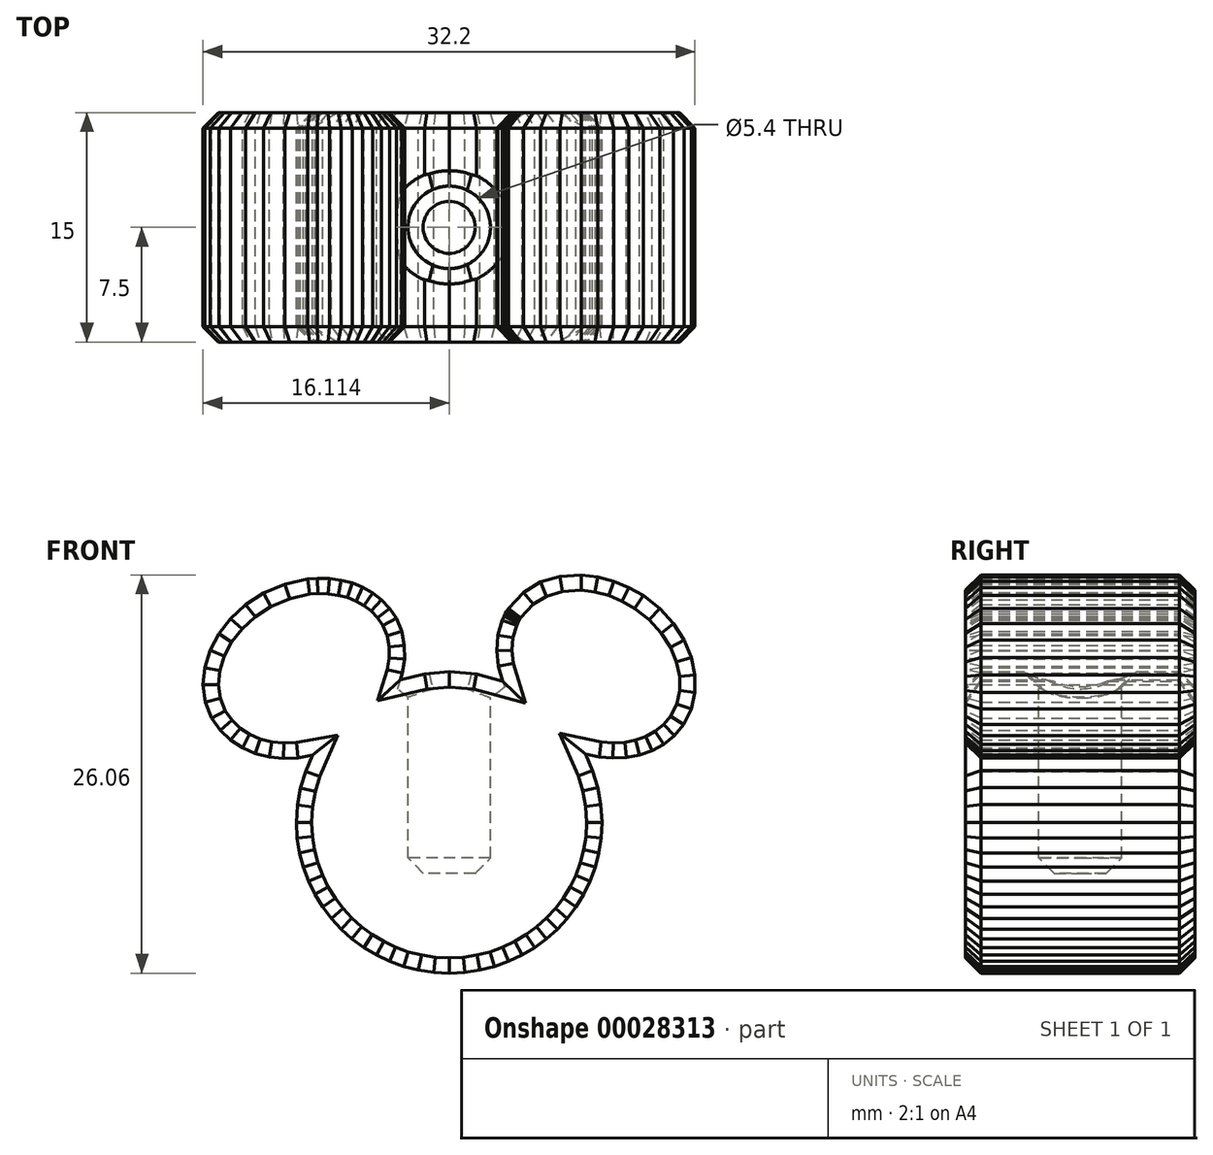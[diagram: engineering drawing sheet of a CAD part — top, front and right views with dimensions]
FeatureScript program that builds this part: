
annotation { "Feature Type Name" : "Feature", "Feature Type Description" : "" }
export const myFeature = defineFeature(function(context is Context, id is Id, definition is map)
    precondition{}
    {
        {
            var Q0;
            Q0=qCreatedBy(makeId("Front.planeOp"),FACE);
            var sketch = newSketch(context, id + "F0", { "sketchPlane" : qUnion([Q0])});
            skLineSegment(sketch, "E0", {"start": v(8.67, 13.03) * mm, "end": v(9.74, 12.9) * mm});
            skLineSegment(sketch, "E1", {"start": v(9.74, 12.9) * mm, "end": v(10.78, 12.63) * mm});
            skLineSegment(sketch, "E2", {"start": v(10.78, 12.63) * mm, "end": v(11.76, 12.21) * mm});
            skLineSegment(sketch, "E3", {"start": v(11.76, 12.21) * mm, "end": v(12.7, 11.68) * mm});
            skLineSegment(sketch, "E4", {"start": v(12.7, 11.68) * mm, "end": v(13.8, 10.82) * mm});
            skLineSegment(sketch, "E5", {"start": v(13.8, 10.82) * mm, "end": v(14.7, 9.84) * mm});
            skLineSegment(sketch, "E6", {"start": v(14.7, 9.84) * mm, "end": v(15.38, 8.77) * mm});
            skLineSegment(sketch, "E7", {"start": v(15.38, 8.77) * mm, "end": v(15.85, 7.64) * mm});
            skLineSegment(sketch, "E8", {"start": v(15.85, 7.64) * mm, "end": v(16.1, 6.48) * mm});
            skLineSegment(sketch, "E9", {"start": v(16.1, 6.48) * mm, "end": v(16.1, 5.34) * mm});
            skLineSegment(sketch, "E10", {"start": v(16.1, 5.34) * mm, "end": v(15.85, 4.25) * mm});
            skLineSegment(sketch, "E11", {"start": v(15.85, 4.25) * mm, "end": v(15.35, 3.24) * mm});
            skLineSegment(sketch, "E12", {"start": v(15.35, 3.24) * mm, "end": v(14.75, 2.52) * mm});
            skLineSegment(sketch, "E13", {"start": v(14.75, 2.52) * mm, "end": v(14.06, 1.96) * mm});
            skLineSegment(sketch, "E14", {"start": v(14.06, 1.96) * mm, "end": v(13.3, 1.53) * mm});
            skLineSegment(sketch, "E15", {"start": v(13.3, 1.53) * mm, "end": v(12.48, 1.25) * mm});
            skLineSegment(sketch, "E16", {"start": v(12.48, 1.25) * mm, "end": v(11.61, 1.09) * mm});
            skLineSegment(sketch, "E17", {"start": v(11.61, 1.09) * mm, "end": v(10.72, 1.05) * mm});
            skLineSegment(sketch, "E18", {"start": v(10.72, 1.05) * mm, "end": v(9.82, 1.12) * mm});
            skLineSegment(sketch, "E19", {"start": v(9.82, 1.12) * mm, "end": v(8.93, 1.3) * mm});
            skLineSegment(sketch, "E20", {"start": v(8.93, 1.3) * mm, "end": v(9.4, 0.24) * mm});
            skLineSegment(sketch, "E21", {"start": v(9.4, 0.24) * mm, "end": v(9.74, -0.87) * mm});
            skLineSegment(sketch, "E22", {"start": v(9.74, -0.87) * mm, "end": v(9.94, -2) * mm});
            skLineSegment(sketch, "E23", {"start": v(9.94, -2) * mm, "end": v(10.01, -3.17) * mm});
            skLineSegment(sketch, "E24", {"start": v(10.01, -3.17) * mm, "end": v(9.96, -4.18) * mm});
            skLineSegment(sketch, "E25", {"start": v(9.96, -4.18) * mm, "end": v(9.81, -5.16) * mm});
            skLineSegment(sketch, "E26", {"start": v(9.81, -5.16) * mm, "end": v(9.56, -6.1) * mm});
            skLineSegment(sketch, "E27", {"start": v(9.56, -6.1) * mm, "end": v(9.23, -7) * mm});
            skLineSegment(sketch, "E28", {"start": v(9.23, -7) * mm, "end": v(8.8, -7.87) * mm});
            skLineSegment(sketch, "E29", {"start": v(8.8, -7.87) * mm, "end": v(8.3, -8.68) * mm});
            skLineSegment(sketch, "E30", {"start": v(8.3, -8.68) * mm, "end": v(7.73, -9.44) * mm});
            skLineSegment(sketch, "E31", {"start": v(7.73, -9.44) * mm, "end": v(7.08, -10.14) * mm});
            skLineSegment(sketch, "E32", {"start": v(7.08, -10.14) * mm, "end": v(6.37, -10.78) * mm});
            skLineSegment(sketch, "E33", {"start": v(6.37, -10.78) * mm, "end": v(5.6, -11.35) * mm});
            skLineSegment(sketch, "E34", {"start": v(5.6, -11.35) * mm, "end": v(4.78, -11.84) * mm});
            skLineSegment(sketch, "E35", {"start": v(4.78, -11.84) * mm, "end": v(3.9, -12.26) * mm});
            skLineSegment(sketch, "E36", {"start": v(3.9, -12.26) * mm, "end": v(2.99, -12.59) * mm});
            skLineSegment(sketch, "E37", {"start": v(2.99, -12.59) * mm, "end": v(2.03, -12.83) * mm});
            skLineSegment(sketch, "E38", {"start": v(2.03, -12.83) * mm, "end": v(1.04, -12.98) * mm});
            skLineSegment(sketch, "E39", {"start": v(1.04, -12.98) * mm, "end": v(0.01, -13.03) * mm});
            skLineSegment(sketch, "E40", {"start": v(0.01, -13.03) * mm, "end": v(-1, -12.98) * mm});
            skLineSegment(sketch, "E41", {"start": v(-1, -12.98) * mm, "end": v(-2, -12.83) * mm});
            skLineSegment(sketch, "E42", {"start": v(-2, -12.83) * mm, "end": v(-2.96, -12.59) * mm});
            skLineSegment(sketch, "E43", {"start": v(-2.96, -12.59) * mm, "end": v(-3.88, -12.26) * mm});
            skLineSegment(sketch, "E44", {"start": v(-3.88, -12.26) * mm, "end": v(-4.75, -11.84) * mm});
            skLineSegment(sketch, "E45", {"start": v(-4.75, -11.84) * mm, "end": v(-5.58, -11.35) * mm});
            skLineSegment(sketch, "E46", {"start": v(-5.58, -11.35) * mm, "end": v(-6.35, -10.78) * mm});
            skLineSegment(sketch, "E47", {"start": v(-6.35, -10.78) * mm, "end": v(-7.06, -10.14) * mm});
            skLineSegment(sketch, "E48", {"start": v(-7.06, -10.14) * mm, "end": v(-7.7, -9.44) * mm});
            skLineSegment(sketch, "E49", {"start": v(-7.7, -9.44) * mm, "end": v(-8.28, -8.68) * mm});
            skLineSegment(sketch, "E50", {"start": v(-8.28, -8.68) * mm, "end": v(-8.78, -7.87) * mm});
            skLineSegment(sketch, "E51", {"start": v(-8.78, -7.87) * mm, "end": v(-9.2, -7) * mm});
            skLineSegment(sketch, "E52", {"start": v(-9.2, -7) * mm, "end": v(-9.54, -6.1) * mm});
            skLineSegment(sketch, "E53", {"start": v(-9.54, -6.1) * mm, "end": v(-9.78, -5.16) * mm});
            skLineSegment(sketch, "E54", {"start": v(-9.78, -5.16) * mm, "end": v(-9.93, -4.18) * mm});
            skLineSegment(sketch, "E55", {"start": v(-9.93, -4.18) * mm, "end": v(-9.99, -3.17) * mm});
            skLineSegment(sketch, "E56", {"start": v(-9.99, -3.17) * mm, "end": v(-9.92, -2.03) * mm});
            skLineSegment(sketch, "E57", {"start": v(-9.92, -2.03) * mm, "end": v(-9.72, -0.9) * mm});
            skLineSegment(sketch, "E58", {"start": v(-9.72, -0.9) * mm, "end": v(-9.38, 0.18) * mm});
            skLineSegment(sketch, "E59", {"start": v(-9.38, 0.18) * mm, "end": v(-8.94, 1.23) * mm});
            skLineSegment(sketch, "E60", {"start": v(-8.94, 1.23) * mm, "end": v(-9.89, 1.06) * mm});
            skLineSegment(sketch, "E61", {"start": v(-9.89, 1.06) * mm, "end": v(-10.84, 1.03) * mm});
            skLineSegment(sketch, "E62", {"start": v(-10.84, 1.03) * mm, "end": v(-11.77, 1.12) * mm});
            skLineSegment(sketch, "E63", {"start": v(-11.77, 1.12) * mm, "end": v(-12.67, 1.35) * mm});
            skLineSegment(sketch, "E64", {"start": v(-12.67, 1.35) * mm, "end": v(-13.52, 1.71) * mm});
            skLineSegment(sketch, "E65", {"start": v(-13.52, 1.71) * mm, "end": v(-14.3, 2.22) * mm});
            skLineSegment(sketch, "E66", {"start": v(-14.3, 2.22) * mm, "end": v(-14.97, 2.87) * mm});
            skLineSegment(sketch, "E67", {"start": v(-14.97, 2.87) * mm, "end": v(-15.54, 3.67) * mm});
            skLineSegment(sketch, "E68", {"start": v(-15.54, 3.67) * mm, "end": v(-15.95, 4.72) * mm});
            skLineSegment(sketch, "E69", {"start": v(-15.95, 4.72) * mm, "end": v(-16.1, 5.83) * mm});
            skLineSegment(sketch, "E70", {"start": v(-16.1, 5.83) * mm, "end": v(-15.99, 6.97) * mm});
            skLineSegment(sketch, "E71", {"start": v(-15.99, 6.97) * mm, "end": v(-15.64, 8.1) * mm});
            skLineSegment(sketch, "E72", {"start": v(-15.64, 8.1) * mm, "end": v(-15.07, 9.17) * mm});
            skLineSegment(sketch, "E73", {"start": v(-15.07, 9.17) * mm, "end": v(-14.29, 10.18) * mm});
            skLineSegment(sketch, "E74", {"start": v(-14.29, 10.18) * mm, "end": v(-13.3, 11.08) * mm});
            skLineSegment(sketch, "E75", {"start": v(-13.3, 11.08) * mm, "end": v(-12.14, 11.84) * mm});
            skLineSegment(sketch, "E76", {"start": v(-12.14, 11.84) * mm, "end": v(-10.74, 12.44) * mm});
            skLineSegment(sketch, "E77", {"start": v(-10.74, 12.44) * mm, "end": v(-9.26, 12.77) * mm});
            skLineSegment(sketch, "E78", {"start": v(-9.26, 12.77) * mm, "end": v(-8.62, 12.82) * mm});
            skLineSegment(sketch, "E79", {"start": v(-8.62, 12.82) * mm, "end": v(-7.83, 12.8) * mm});
            skLineSegment(sketch, "E80", {"start": v(-7.83, 12.8) * mm, "end": v(-7.07, 12.69) * mm});
            skLineSegment(sketch, "E81", {"start": v(-7.07, 12.69) * mm, "end": v(-6.34, 12.5) * mm});
            skLineSegment(sketch, "E82", {"start": v(-6.34, 12.5) * mm, "end": v(-5.65, 12.23) * mm});
            skLineSegment(sketch, "E83", {"start": v(-5.65, 12.23) * mm, "end": v(-5, 11.86) * mm});
            skLineSegment(sketch, "E84", {"start": v(-5, 11.86) * mm, "end": v(-4.42, 11.4) * mm});
            skLineSegment(sketch, "E85", {"start": v(-4.42, 11.4) * mm, "end": v(-3.9, 10.85) * mm});
            skLineSegment(sketch, "E86", {"start": v(-3.9, 10.85) * mm, "end": v(-3.45, 10.19) * mm});
            skLineSegment(sketch, "E87", {"start": v(-3.45, 10.19) * mm, "end": v(-3.1, 9.33) * mm});
            skLineSegment(sketch, "E88", {"start": v(-3.1, 9.33) * mm, "end": v(-2.92, 8.43) * mm});
            skLineSegment(sketch, "E89", {"start": v(-2.92, 8.43) * mm, "end": v(-2.91, 7.52) * mm});
            skLineSegment(sketch, "E90", {"start": v(-2.91, 7.52) * mm, "end": v(-3.06, 6.6) * mm});
            skLineSegment(sketch, "E91", {"start": v(-3.06, 6.6) * mm, "end": v(-3.2, 6.18) * mm});
            skLineSegment(sketch, "E92", {"start": v(-3.2, 6.18) * mm, "end": v(-1.61, 6.56) * mm});
            skLineSegment(sketch, "E93", {"start": v(-1.61, 6.56) * mm, "end": v(0.01, 6.7) * mm});
            skLineSegment(sketch, "E94", {"start": v(0.01, 6.7) * mm, "end": v(1.8, 6.54) * mm});
            skLineSegment(sketch, "E95", {"start": v(1.8, 6.54) * mm, "end": v(3.52, 6.07) * mm});
            skLineSegment(sketch, "E96", {"start": v(3.52, 6.07) * mm, "end": v(3.23, 7.05) * mm});
            skLineSegment(sketch, "E97", {"start": v(3.23, 7.05) * mm, "end": v(3.12, 8.08) * mm});
            skLineSegment(sketch, "E98", {"start": v(3.12, 8.08) * mm, "end": v(3.2, 9.1) * mm});
            skLineSegment(sketch, "E99", {"start": v(3.2, 9.1) * mm, "end": v(3.5, 10.08) * mm});
            skLineSegment(sketch, "E100", {"start": v(3.5, 10.08) * mm, "end": v(3.6, 10.31) * mm});
            skLineSegment(sketch, "E101", {"start": v(3.6, 10.31) * mm, "end": v(3.69, 10.49) * mm});
            skLineSegment(sketch, "E102", {"start": v(3.69, 10.49) * mm, "end": v(3.78, 10.65) * mm});
            skLineSegment(sketch, "E103", {"start": v(3.78, 10.65) * mm, "end": v(3.9, 10.83) * mm});
            skLineSegment(sketch, "E104", {"start": v(3.9, 10.83) * mm, "end": v(4.87, 11.9) * mm});
            skLineSegment(sketch, "E105", {"start": v(4.87, 11.9) * mm, "end": v(5.98, 12.57) * mm});
            skLineSegment(sketch, "E106", {"start": v(5.98, 12.57) * mm, "end": v(7.25, 12.92) * mm});
            skLineSegment(sketch, "E107", {"start": v(7.25, 12.92) * mm, "end": v(8.67, 13.03) * mm});
            skSolve(sketch);
        }
        {
            var Q0;
            Q0 = qSketchRegion(id + "F0", true);
            extrude(context, id + "F1", {"entities" : qUnion([Q0]), "depth" : 15 * mm});
        }
        {
            var Q0;
            Q0=makeQuery(id+"F1.opExtrude","CAP_FACE",FACE,{"disambiguationData":[OSD([sQuery(id+"F0.wireOp",EDGE,"E0"),sQuery(id+"F0.wireOp",EDGE,"E1"),sQuery(id+"F0.wireOp",EDGE,"E2"),sQuery(id+"F0.wireOp",EDGE,"E3"),sQuery(id+"F0.wireOp",EDGE,"E4"),sQuery(id+"F0.wireOp",EDGE,"E5"),sQuery(id+"F0.wireOp",EDGE,"E6"),sQuery(id+"F0.wireOp",EDGE,"E7"),sQuery(id+"F0.wireOp",EDGE,"E8"),sQuery(id+"F0.wireOp",EDGE,"E9"),sQuery(id+"F0.wireOp",EDGE,"E10"),sQuery(id+"F0.wireOp",EDGE,"E11"),sQuery(id+"F0.wireOp",EDGE,"E12"),sQuery(id+"F0.wireOp",EDGE,"E13"),sQuery(id+"F0.wireOp",EDGE,"E14"),sQuery(id+"F0.wireOp",EDGE,"E15"),sQuery(id+"F0.wireOp",EDGE,"E16"),sQuery(id+"F0.wireOp",EDGE,"E17"),sQuery(id+"F0.wireOp",EDGE,"E18"),sQuery(id+"F0.wireOp",EDGE,"E19"),sQuery(id+"F0.wireOp",EDGE,"E20"),sQuery(id+"F0.wireOp",EDGE,"E21"),sQuery(id+"F0.wireOp",EDGE,"E22"),sQuery(id+"F0.wireOp",EDGE,"E23"),sQuery(id+"F0.wireOp",EDGE,"E24"),sQuery(id+"F0.wireOp",EDGE,"E25"),sQuery(id+"F0.wireOp",EDGE,"E26"),sQuery(id+"F0.wireOp",EDGE,"E27"),sQuery(id+"F0.wireOp",EDGE,"E28"),sQuery(id+"F0.wireOp",EDGE,"E29"),sQuery(id+"F0.wireOp",EDGE,"E30"),sQuery(id+"F0.wireOp",EDGE,"E31"),sQuery(id+"F0.wireOp",EDGE,"E32"),sQuery(id+"F0.wireOp",EDGE,"E33"),sQuery(id+"F0.wireOp",EDGE,"E34"),sQuery(id+"F0.wireOp",EDGE,"E35"),sQuery(id+"F0.wireOp",EDGE,"E36"),sQuery(id+"F0.wireOp",EDGE,"E37"),sQuery(id+"F0.wireOp",EDGE,"E38"),sQuery(id+"F0.wireOp",EDGE,"E39"),sQuery(id+"F0.wireOp",EDGE,"E40"),sQuery(id+"F0.wireOp",EDGE,"E41"),sQuery(id+"F0.wireOp",EDGE,"E42"),sQuery(id+"F0.wireOp",EDGE,"E43"),sQuery(id+"F0.wireOp",EDGE,"E44"),sQuery(id+"F0.wireOp",EDGE,"E45"),sQuery(id+"F0.wireOp",EDGE,"E46"),sQuery(id+"F0.wireOp",EDGE,"E47"),sQuery(id+"F0.wireOp",EDGE,"E48"),sQuery(id+"F0.wireOp",EDGE,"E49"),sQuery(id+"F0.wireOp",EDGE,"E50"),sQuery(id+"F0.wireOp",EDGE,"E51"),sQuery(id+"F0.wireOp",EDGE,"E52"),sQuery(id+"F0.wireOp",EDGE,"E53"),sQuery(id+"F0.wireOp",EDGE,"E54"),sQuery(id+"F0.wireOp",EDGE,"E55"),sQuery(id+"F0.wireOp",EDGE,"E56"),sQuery(id+"F0.wireOp",EDGE,"E57"),sQuery(id+"F0.wireOp",EDGE,"E58"),sQuery(id+"F0.wireOp",EDGE,"E59"),sQuery(id+"F0.wireOp",EDGE,"E60"),sQuery(id+"F0.wireOp",EDGE,"E61"),sQuery(id+"F0.wireOp",EDGE,"E62"),sQuery(id+"F0.wireOp",EDGE,"E63"),sQuery(id+"F0.wireOp",EDGE,"E64"),sQuery(id+"F0.wireOp",EDGE,"E65"),sQuery(id+"F0.wireOp",EDGE,"E66"),sQuery(id+"F0.wireOp",EDGE,"E67"),sQuery(id+"F0.wireOp",EDGE,"E68"),sQuery(id+"F0.wireOp",EDGE,"E69"),sQuery(id+"F0.wireOp",EDGE,"E70"),sQuery(id+"F0.wireOp",EDGE,"E71"),sQuery(id+"F0.wireOp",EDGE,"E72"),sQuery(id+"F0.wireOp",EDGE,"E73"),sQuery(id+"F0.wireOp",EDGE,"E74"),sQuery(id+"F0.wireOp",EDGE,"E75"),sQuery(id+"F0.wireOp",EDGE,"E76"),sQuery(id+"F0.wireOp",EDGE,"E77"),sQuery(id+"F0.wireOp",EDGE,"E78"),sQuery(id+"F0.wireOp",EDGE,"E79"),sQuery(id+"F0.wireOp",EDGE,"E80"),sQuery(id+"F0.wireOp",EDGE,"E81"),sQuery(id+"F0.wireOp",EDGE,"E82"),sQuery(id+"F0.wireOp",EDGE,"E83"),sQuery(id+"F0.wireOp",EDGE,"E84"),sQuery(id+"F0.wireOp",EDGE,"E85"),sQuery(id+"F0.wireOp",EDGE,"E86"),sQuery(id+"F0.wireOp",EDGE,"E87"),sQuery(id+"F0.wireOp",EDGE,"E88"),sQuery(id+"F0.wireOp",EDGE,"E89"),sQuery(id+"F0.wireOp",EDGE,"E90"),sQuery(id+"F0.wireOp",EDGE,"E91"),sQuery(id+"F0.wireOp",EDGE,"E92"),sQuery(id+"F0.wireOp",EDGE,"E93"),sQuery(id+"F0.wireOp",EDGE,"E94"),sQuery(id+"F0.wireOp",EDGE,"E95"),sQuery(id+"F0.wireOp",EDGE,"E96"),sQuery(id+"F0.wireOp",EDGE,"E97"),sQuery(id+"F0.wireOp",EDGE,"E98"),sQuery(id+"F0.wireOp",EDGE,"E99"),sQuery(id+"F0.wireOp",EDGE,"E100"),sQuery(id+"F0.wireOp",EDGE,"E101"),sQuery(id+"F0.wireOp",EDGE,"E102"),sQuery(id+"F0.wireOp",EDGE,"E103"),sQuery(id+"F0.wireOp",EDGE,"E104"),sQuery(id+"F0.wireOp",EDGE,"E105"),sQuery(id+"F0.wireOp",EDGE,"E106"),sQuery(id+"F0.wireOp",EDGE,"E107")])],"isStart":false});
            var Q1;
            Q1=makeQuery(id+"F1.opExtrude","CAP_FACE",FACE,{"disambiguationData":[OSD([sQuery(id+"F0.wireOp",EDGE,"E0"),sQuery(id+"F0.wireOp",EDGE,"E1"),sQuery(id+"F0.wireOp",EDGE,"E2"),sQuery(id+"F0.wireOp",EDGE,"E3"),sQuery(id+"F0.wireOp",EDGE,"E4"),sQuery(id+"F0.wireOp",EDGE,"E5"),sQuery(id+"F0.wireOp",EDGE,"E6"),sQuery(id+"F0.wireOp",EDGE,"E7"),sQuery(id+"F0.wireOp",EDGE,"E8"),sQuery(id+"F0.wireOp",EDGE,"E9"),sQuery(id+"F0.wireOp",EDGE,"E10"),sQuery(id+"F0.wireOp",EDGE,"E11"),sQuery(id+"F0.wireOp",EDGE,"E12"),sQuery(id+"F0.wireOp",EDGE,"E13"),sQuery(id+"F0.wireOp",EDGE,"E14"),sQuery(id+"F0.wireOp",EDGE,"E15"),sQuery(id+"F0.wireOp",EDGE,"E16"),sQuery(id+"F0.wireOp",EDGE,"E17"),sQuery(id+"F0.wireOp",EDGE,"E18"),sQuery(id+"F0.wireOp",EDGE,"E19"),sQuery(id+"F0.wireOp",EDGE,"E20"),sQuery(id+"F0.wireOp",EDGE,"E21"),sQuery(id+"F0.wireOp",EDGE,"E22"),sQuery(id+"F0.wireOp",EDGE,"E23"),sQuery(id+"F0.wireOp",EDGE,"E24"),sQuery(id+"F0.wireOp",EDGE,"E25"),sQuery(id+"F0.wireOp",EDGE,"E26"),sQuery(id+"F0.wireOp",EDGE,"E27"),sQuery(id+"F0.wireOp",EDGE,"E28"),sQuery(id+"F0.wireOp",EDGE,"E29"),sQuery(id+"F0.wireOp",EDGE,"E30"),sQuery(id+"F0.wireOp",EDGE,"E31"),sQuery(id+"F0.wireOp",EDGE,"E32"),sQuery(id+"F0.wireOp",EDGE,"E33"),sQuery(id+"F0.wireOp",EDGE,"E34"),sQuery(id+"F0.wireOp",EDGE,"E35"),sQuery(id+"F0.wireOp",EDGE,"E36"),sQuery(id+"F0.wireOp",EDGE,"E37"),sQuery(id+"F0.wireOp",EDGE,"E38"),sQuery(id+"F0.wireOp",EDGE,"E39"),sQuery(id+"F0.wireOp",EDGE,"E40"),sQuery(id+"F0.wireOp",EDGE,"E41"),sQuery(id+"F0.wireOp",EDGE,"E42"),sQuery(id+"F0.wireOp",EDGE,"E43"),sQuery(id+"F0.wireOp",EDGE,"E44"),sQuery(id+"F0.wireOp",EDGE,"E45"),sQuery(id+"F0.wireOp",EDGE,"E46"),sQuery(id+"F0.wireOp",EDGE,"E47"),sQuery(id+"F0.wireOp",EDGE,"E48"),sQuery(id+"F0.wireOp",EDGE,"E49"),sQuery(id+"F0.wireOp",EDGE,"E50"),sQuery(id+"F0.wireOp",EDGE,"E51"),sQuery(id+"F0.wireOp",EDGE,"E52"),sQuery(id+"F0.wireOp",EDGE,"E53"),sQuery(id+"F0.wireOp",EDGE,"E54"),sQuery(id+"F0.wireOp",EDGE,"E55"),sQuery(id+"F0.wireOp",EDGE,"E56"),sQuery(id+"F0.wireOp",EDGE,"E57"),sQuery(id+"F0.wireOp",EDGE,"E58"),sQuery(id+"F0.wireOp",EDGE,"E59"),sQuery(id+"F0.wireOp",EDGE,"E60"),sQuery(id+"F0.wireOp",EDGE,"E61"),sQuery(id+"F0.wireOp",EDGE,"E62"),sQuery(id+"F0.wireOp",EDGE,"E63"),sQuery(id+"F0.wireOp",EDGE,"E64"),sQuery(id+"F0.wireOp",EDGE,"E65"),sQuery(id+"F0.wireOp",EDGE,"E66"),sQuery(id+"F0.wireOp",EDGE,"E67"),sQuery(id+"F0.wireOp",EDGE,"E68"),sQuery(id+"F0.wireOp",EDGE,"E69"),sQuery(id+"F0.wireOp",EDGE,"E70"),sQuery(id+"F0.wireOp",EDGE,"E71"),sQuery(id+"F0.wireOp",EDGE,"E72"),sQuery(id+"F0.wireOp",EDGE,"E73"),sQuery(id+"F0.wireOp",EDGE,"E74"),sQuery(id+"F0.wireOp",EDGE,"E75"),sQuery(id+"F0.wireOp",EDGE,"E76"),sQuery(id+"F0.wireOp",EDGE,"E77"),sQuery(id+"F0.wireOp",EDGE,"E78"),sQuery(id+"F0.wireOp",EDGE,"E79"),sQuery(id+"F0.wireOp",EDGE,"E80"),sQuery(id+"F0.wireOp",EDGE,"E81"),sQuery(id+"F0.wireOp",EDGE,"E82"),sQuery(id+"F0.wireOp",EDGE,"E83"),sQuery(id+"F0.wireOp",EDGE,"E84"),sQuery(id+"F0.wireOp",EDGE,"E85"),sQuery(id+"F0.wireOp",EDGE,"E86"),sQuery(id+"F0.wireOp",EDGE,"E87"),sQuery(id+"F0.wireOp",EDGE,"E88"),sQuery(id+"F0.wireOp",EDGE,"E89"),sQuery(id+"F0.wireOp",EDGE,"E90"),sQuery(id+"F0.wireOp",EDGE,"E91"),sQuery(id+"F0.wireOp",EDGE,"E92"),sQuery(id+"F0.wireOp",EDGE,"E93"),sQuery(id+"F0.wireOp",EDGE,"E94"),sQuery(id+"F0.wireOp",EDGE,"E95"),sQuery(id+"F0.wireOp",EDGE,"E96"),sQuery(id+"F0.wireOp",EDGE,"E97"),sQuery(id+"F0.wireOp",EDGE,"E98"),sQuery(id+"F0.wireOp",EDGE,"E99"),sQuery(id+"F0.wireOp",EDGE,"E100"),sQuery(id+"F0.wireOp",EDGE,"E101"),sQuery(id+"F0.wireOp",EDGE,"E102"),sQuery(id+"F0.wireOp",EDGE,"E103"),sQuery(id+"F0.wireOp",EDGE,"E104"),sQuery(id+"F0.wireOp",EDGE,"E105"),sQuery(id+"F0.wireOp",EDGE,"E106"),sQuery(id+"F0.wireOp",EDGE,"E107")])],"isStart":true});
            chamfer(context, id + "F2", {"entities" : qUnion([Q0, Q1]), "width" : 1 * mm, "tangentPropagation" : true});
        }
        {
            var Q0;
            Q0=qCreatedBy(makeId("Top.planeOp"),FACE);
            var sketch = newSketch(context, id + "F3", { "sketchPlane" : qUnion([Q0])});
            skLineSegment(sketch, "E108.0", {"start": v(0.01, -14) * mm, "end": v(0.01, -1) * mm, "construction": true});
            skCircle(sketch, "E109", {"center": v(0.01, -7.5) * mm, "radius": 2.7 * mm});
            skSolve(sketch);
        }
        {
            var Q0;
            Q0 = qSketchRegion(id + "F3", true);
            extrude(context, id + "F4", {"entities" : qUnion([Q0]), "operationType" : NewBodyOperationType.REMOVE, "oppositeDirection" : true, "depth" : 6.5 * mm, "hasSecondDirection" : true, "secondDirectionOppositeDirection" : false, "secondDirectionDepth" : 8 * mm});
        }
        {
            var Q0;
            Q0=makeQuery(id+"F4.boolean.opBoolean","COPY",EDGE,{"derivedFrom":makeQuery(id+"F4.opExtrude","CAP_EDGE",EDGE,{"disambiguationData":[OSD([sQuery(id+"F3.wireOp",EDGE,"E109")])],"isStart":false})});
            var Q1;
            Q1=makeQuery(id+"F4.boolean.opBoolean","INTERSECT",EDGE,{"disambiguationData":[OD(1.0)],"derivedFrom":[makeQuery(id+"F1.opExtrude","SWEPT_FACE",FACE,{"disambiguationData":[OSD([sQuery(id+"F0.wireOp",EDGE,"E93")])]}),makeQuery(id+"F4.opExtrude","SWEPT_FACE",FACE,{"disambiguationData":[OSD([sQuery(id+"F3.wireOp",EDGE,"E109")])]})]});
            var Q2;
            Q2=makeQuery(id+"F4.boolean.opBoolean","INTERSECT",EDGE,{"derivedFrom":[makeQuery(id+"F1.opExtrude","SWEPT_FACE",FACE,{"disambiguationData":[OSD([sQuery(id+"F0.wireOp",EDGE,"E92")])]}),makeQuery(id+"F4.opExtrude","SWEPT_FACE",FACE,{"disambiguationData":[OSD([sQuery(id+"F3.wireOp",EDGE,"E109")])]})]});
            var Q3;
            Q3=makeQuery(id+"F4.boolean.opBoolean","INTERSECT",EDGE,{"disambiguationData":[OD(0.0)],"derivedFrom":[makeQuery(id+"F1.opExtrude","SWEPT_FACE",FACE,{"disambiguationData":[OSD([sQuery(id+"F0.wireOp",EDGE,"E93")])]}),makeQuery(id+"F4.opExtrude","SWEPT_FACE",FACE,{"disambiguationData":[OSD([sQuery(id+"F3.wireOp",EDGE,"E109")])]})]});
            var Q4;
            Q4=makeQuery(id+"F4.boolean.opBoolean","INTERSECT",EDGE,{"disambiguationData":[OD(0.0)],"derivedFrom":[makeQuery(id+"F1.opExtrude","SWEPT_FACE",FACE,{"disambiguationData":[OSD([sQuery(id+"F0.wireOp",EDGE,"E94")])]}),makeQuery(id+"F4.opExtrude","SWEPT_FACE",FACE,{"disambiguationData":[OSD([sQuery(id+"F3.wireOp",EDGE,"E109")])]})]});
            var Q5;
            Q5=makeQuery(id+"F4.boolean.opBoolean","INTERSECT",EDGE,{"derivedFrom":[makeQuery(id+"F1.opExtrude","SWEPT_FACE",FACE,{"disambiguationData":[OSD([sQuery(id+"F0.wireOp",EDGE,"E95")])]}),makeQuery(id+"F4.opExtrude","SWEPT_FACE",FACE,{"disambiguationData":[OSD([sQuery(id+"F3.wireOp",EDGE,"E109")])]})]});
            var Q6;
            Q6=makeQuery(id+"F4.boolean.opBoolean","INTERSECT",EDGE,{"disambiguationData":[OD(1.0)],"derivedFrom":[makeQuery(id+"F1.opExtrude","SWEPT_FACE",FACE,{"disambiguationData":[OSD([sQuery(id+"F0.wireOp",EDGE,"E94")])]}),makeQuery(id+"F4.opExtrude","SWEPT_FACE",FACE,{"disambiguationData":[OSD([sQuery(id+"F3.wireOp",EDGE,"E109")])]})]});
            chamfer(context, id + "F5", {"entities" : qUnion([Q0, Q1, Q2, Q3, Q4, Q5, Q6]), "width" : 1 * mm, "tangentPropagation" : true});
        }
    });
